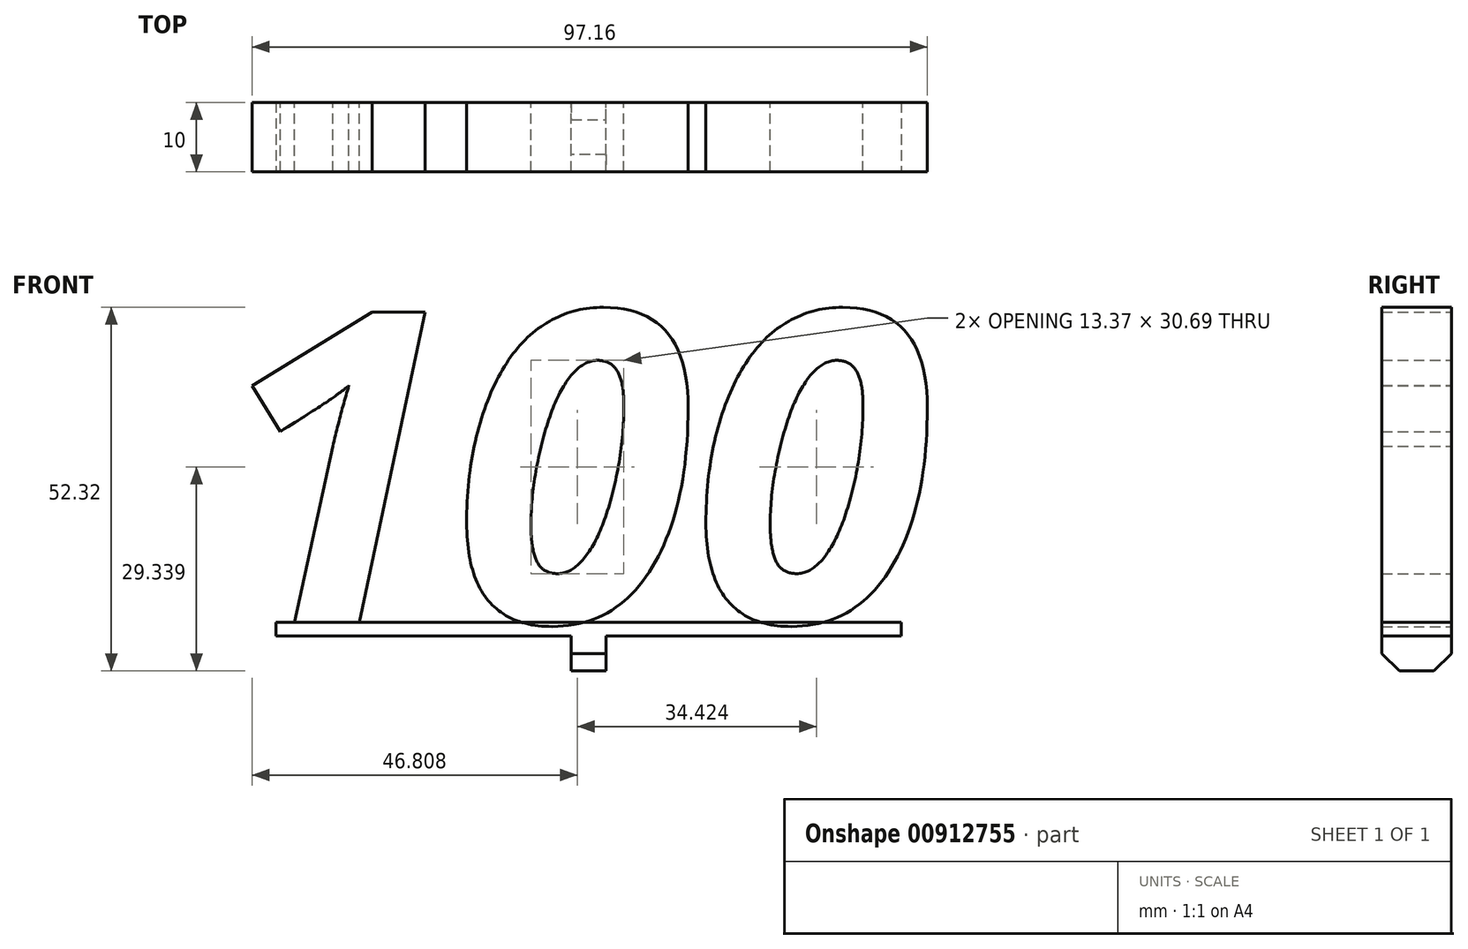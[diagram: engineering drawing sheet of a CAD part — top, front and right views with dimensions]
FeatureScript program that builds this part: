
annotation { "Feature Type Name" : "Feature", "Feature Type Description" : "" }
export const myFeature = defineFeature(function(context is Context, id is Id, definition is map)
    precondition{}
    {
        {
            var Q0;
            Q0=qCreatedBy(makeId("Front.planeOp"),FACE);
            var sketch = newSketch(context, id + "F0", { "sketchPlane" : qUnion([Q0])});
            skText(sketch, "E0", { "text": "100", "fontName": "OpenSans-BoldItalic.ttf"});
            const initialGuessF0  = {"E0": [-0.054, 0, 1, 0, 0.045]};
            skSetInitialGuess(sketch, initialGuessF0);
            skSolve(sketch);
        }
        {
            var Q0;
            Q0=qSketchRegion(id+"F0",true);
            extrude(context, id + "F1", {"entities" : qUnion([Q0]), "endBound" : BoundingType.SYMMETRIC, "depth" : 10 * mm, "offsetDistance" : 25 * mm});
        }
        {
            var Q0;
            Q0=qCreatedBy(makeId("Top.planeOp"),FACE);
            var sketch = newSketch(context, id + "F2", { "sketchPlane" : qUnion([Q0])});
            skLineSegment(sketch, "E1.bottom", {"start": v(-45, 5) * mm, "end": v(45, 5) * mm});
            skLineSegment(sketch, "E1.top", {"start": v(-45, -5) * mm, "end": v(45, -5) * mm});
            skLineSegment(sketch, "E1.left", {"start": v(-45, 5) * mm, "end": v(-45, -5) * mm});
            skLineSegment(sketch, "E1.right", {"start": v(45, 5) * mm, "end": v(45, -5) * mm});
            skSolve(sketch);
        }
        {
            var Q0;
            Q0=qSketchRegion(id+"F2",true);
            extrude(context, id + "F3", {"entities" : qUnion([Q0]), "oppositeDirection" : true, "depth" : 2 * mm, "offsetDistance" : 25 * mm});
        }
        {
            var Q0;
            Q0=makeQuery(id+"F3.opExtrude","CAP_FACE",FACE,{"disambiguationData":[OSD([sQuery(id+"F2.wireOp",EDGE,"E1.bottom"),sQuery(id+"F2.wireOp",EDGE,"E1.top"),sQuery(id+"F2.wireOp",EDGE,"E1.left"),sQuery(id+"F2.wireOp",EDGE,"E1.right")])],"isStart":false});
            var sketch = newSketch(context, id + "F4", { "sketchPlane" : qUnion([Q0])});
            skLineSegment(sketch, "E2.bottom", {"start": v(2.5, 5) * mm, "end": v(-2.5, 5) * mm});
            skLineSegment(sketch, "E2.top", {"start": v(2.5, -5) * mm, "end": v(-2.5, -5) * mm});
            skLineSegment(sketch, "E2.left", {"start": v(2.5, 5) * mm, "end": v(2.5, -5) * mm});
            skLineSegment(sketch, "E2.right", {"start": v(-2.5, 5) * mm, "end": v(-2.5, -5) * mm});
            skLineSegment(sketch, "E3", {"start": v(0, 5) * mm, "end": v(0, -5) * mm, "construction": true});
            skSolve(sketch);
        }
        {
            var Q0;
            Q0=qSketchRegion(id+"F4",true);
            extrude(context, id + "F5", {"entities" : qUnion([Q0]), "operationType" : NewBodyOperationType.ADD, "depth" : 5 * mm, "offsetDistance" : 25 * mm});
        }
        {
            var Q0;
            Q0=makeQuery(id+"F5.opExtrude","CAP_EDGE",EDGE,{"disambiguationData":[OSD([sQuery(id+"F4.wireOp",EDGE,"E2.bottom")])],"isStart":false});
            var Q1;
            Q1=makeQuery(id+"F5.opExtrude","CAP_EDGE",EDGE,{"disambiguationData":[OSD([sQuery(id+"F4.wireOp",EDGE,"E2.top")])],"isStart":false});
            chamfer(context, id + "F6", {"entities" : qUnion([Q0, Q1]), "width" : 2.5 * mm, "tangentPropagation" : true});
        }
    });
